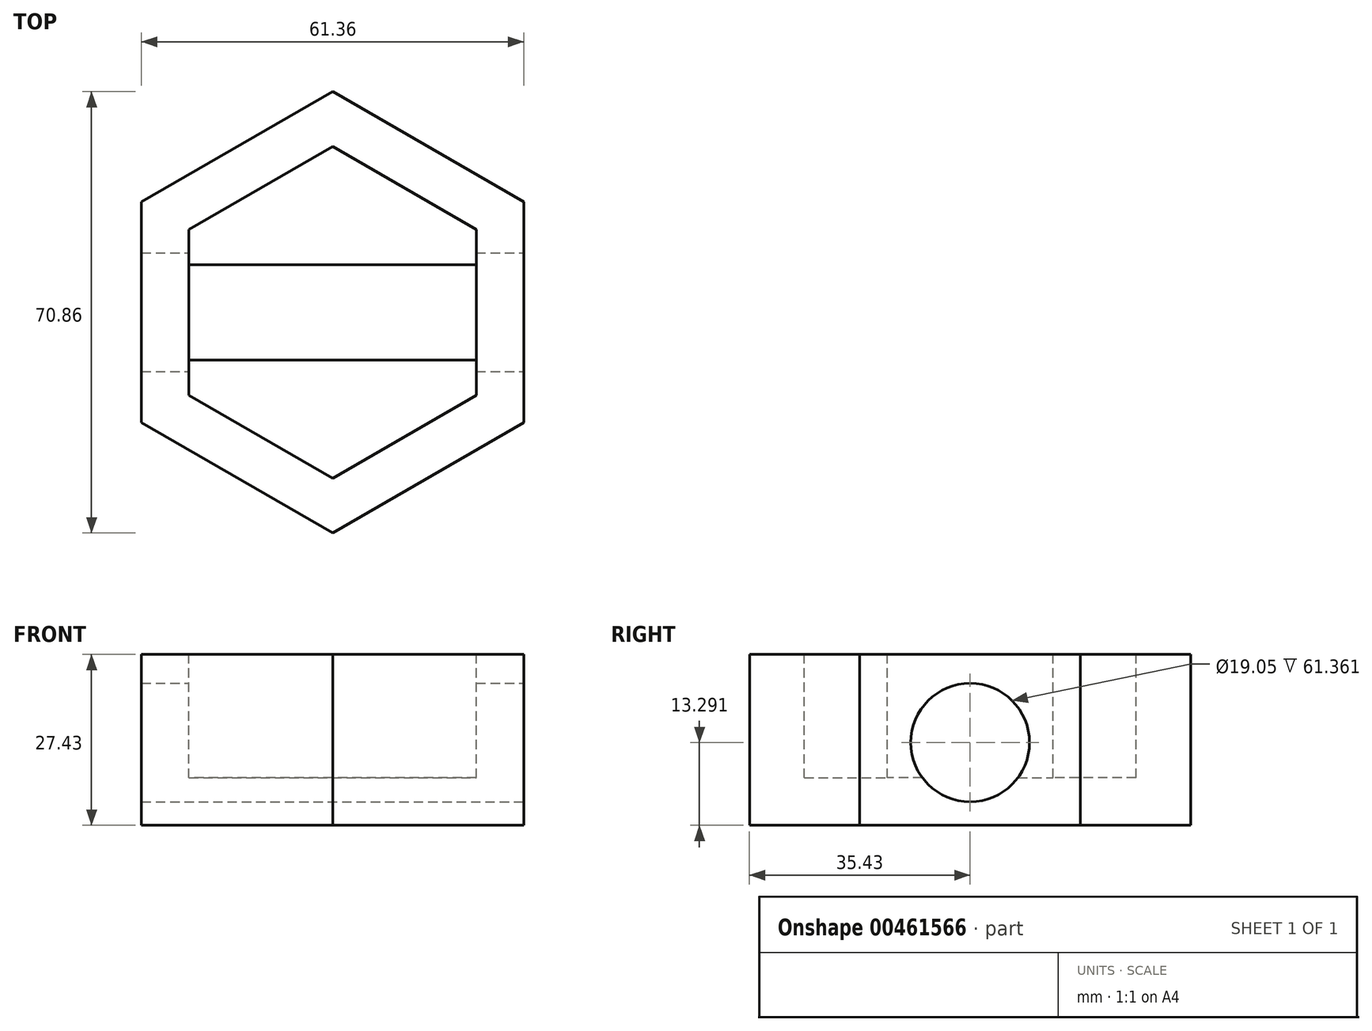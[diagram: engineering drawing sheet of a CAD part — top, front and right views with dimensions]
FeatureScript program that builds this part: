
annotation { "Feature Type Name" : "Feature", "Feature Type Description" : "" }
export const myFeature = defineFeature(function(context is Context, id is Id, definition is map)
    precondition{}
    {
        {
            var Q0;
            Q0=qCreatedBy(makeId("Right.planeOp"),FACE);
            var sketch = newSketch(context, id + "F0", { "sketchPlane" : qUnion([Q0])});
            skPoint(sketch, "E0.middle", {"position": v(0, 0) * mm});
            skLineSegment(sketch, "E1.bottom", {"start": v(-17.72, 0) * mm, "end": v(18.12, 0) * mm});
            skLineSegment(sketch, "E1.top", {"start": v(-17.72, -26.77) * mm, "end": v(18.12, -26.77) * mm});
            skLineSegment(sketch, "E1.left", {"start": v(-17.72, 0) * mm, "end": v(-17.72, -26.77) * mm});
            skLineSegment(sketch, "E1.right", {"start": v(18.12, 0) * mm, "end": v(18.12, -26.77) * mm});
            skCircle(sketch, "E2", {"center": v(0, -14.14) * mm, "radius": 7.42 * mm});
            skSolve(sketch);
        }
        {
            var Q0;
            Q0=qCreatedBy(makeId("Top.planeOp"),FACE);
            var sketch = newSketch(context, id + "F1", { "sketchPlane" : qUnion([Q0])});
            skCircle(sketch, "E3.cCircle", {"center": v(-30.68, 0) * mm, "radius": 30.68 * mm, "construction": true});
            skLineSegment(sketch, "E3.0", {"start": v(0, 17.71) * mm, "end": v(0, -17.71) * mm});
            skLineSegment(sketch, "E3.1", {"start": v(0, -17.71) * mm, "end": v(-30.68, -35.43) * mm});
            skLineSegment(sketch, "E3.2", {"start": v(-30.68, -35.43) * mm, "end": v(-61.36, -17.71) * mm});
            skLineSegment(sketch, "E3.3", {"start": v(-61.36, -17.71) * mm, "end": v(-61.36, 17.71) * mm});
            skLineSegment(sketch, "E3.4", {"start": v(-61.36, 17.71) * mm, "end": v(-30.68, 35.43) * mm});
            skLineSegment(sketch, "E3.5", {"start": v(-30.68, 35.43) * mm, "end": v(0, 17.71) * mm});
            skPoint(sketch, "E3.0.midPoint", {"position": v(0, 0) * mm});
            skSolve(sketch);
        }
        {
            var Q0;
            Q0=makeQuery(id+"F1.imprint","IMPRINT",FACE,{"disambiguationData":[TD([[makeQuery(id+"F1.imprint","IMPRINT",EDGE,{"derivedFrom":sQuery(id+"F1.wireOp",EDGE,"E3.0")}),-1.0]])]});
            extrude(context, id + "F2", {"entities" : qUnion([Q0]), "oppositeDirection" : true, "depth" : 27.43 * mm});
        }
        {
            var Q0;
            Q0=makeQuery(id+"F2.opExtrude","CAP_FACE",FACE,{"disambiguationData":[OSD([sQuery(id+"F1.wireOp",EDGE,"E3.0"),sQuery(id+"F1.wireOp",EDGE,"E3.1"),sQuery(id+"F1.wireOp",EDGE,"E3.2"),sQuery(id+"F1.wireOp",EDGE,"E3.3"),sQuery(id+"F1.wireOp",EDGE,"E3.4"),sQuery(id+"F1.wireOp",EDGE,"E3.5")])],"isStart":true});
            shell(context, id + "F3", {"entities" : qUnion([Q0]), "thickness" : 7.62 * mm});
        }
        {
            var Q0;
            Q0=sQuery(id+"F0.wireOp",VERTEX,"E2.center");
            var Q1;
            Q1=makeQuery(id+"F2.opExtrude","SWEPT_BODY",BODY,{"disambiguationData":[OSD([sQuery(id+"F1.wireOp",EDGE,"E3.0"),sQuery(id+"F1.wireOp",EDGE,"E3.1"),sQuery(id+"F1.wireOp",EDGE,"E3.2"),sQuery(id+"F1.wireOp",EDGE,"E3.3"),sQuery(id+"F1.wireOp",EDGE,"E3.4"),sQuery(id+"F1.wireOp",EDGE,"E3.5")])]});
            hole(context, id + "F4", {"style" : HoleStyle.SIMPLE, "endStyle" : HoleEndStyle.THROUGH, "holeDiameter" : 19.05 * mm, "isTappedThrough" : true, "tappedDepth" : 12.7 * mm, "tapClearance" : 3, "locations" : qUnion([Q0]), "scope" : qUnion([Q1])});
        }
    });
